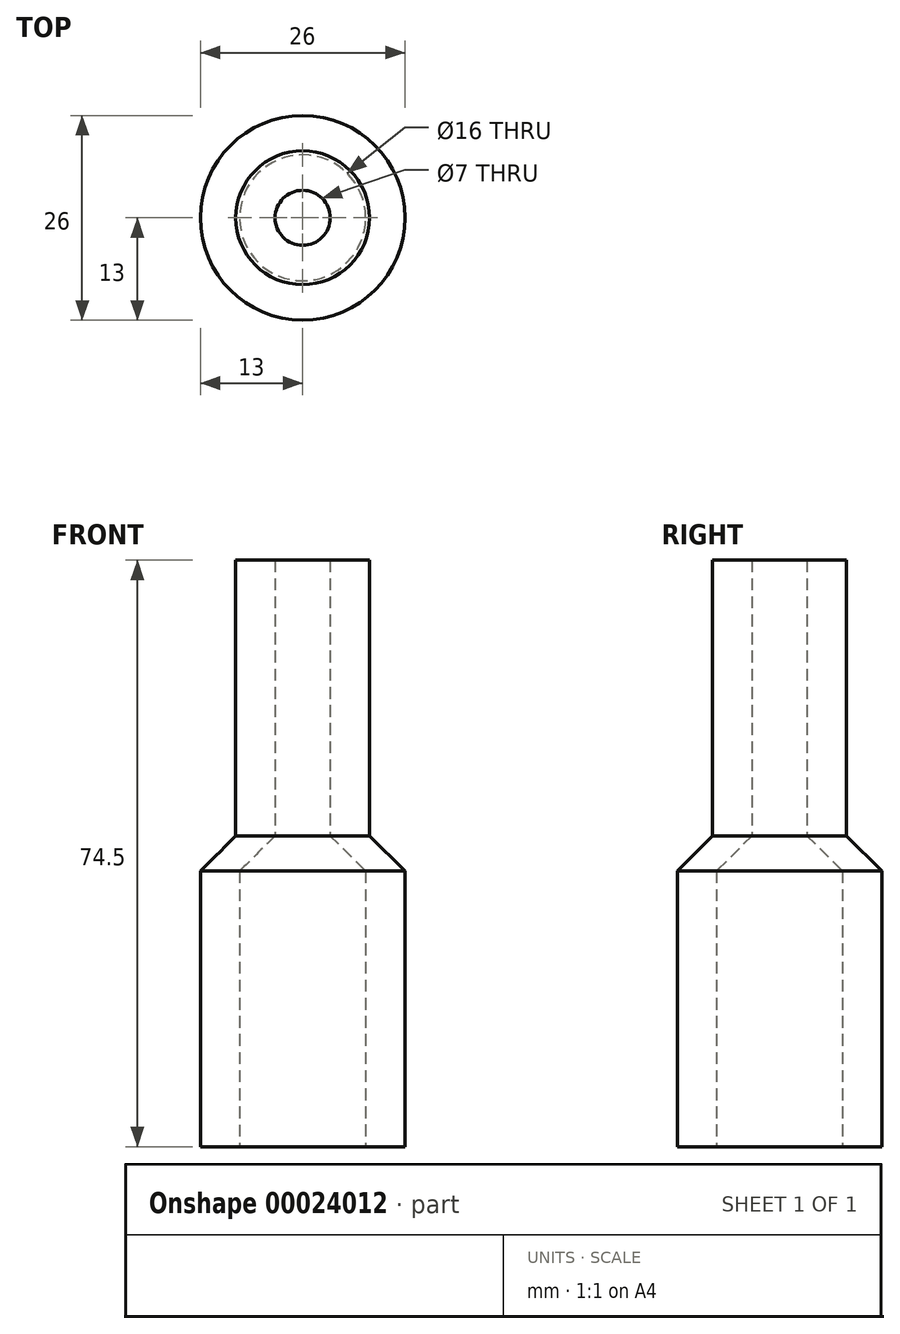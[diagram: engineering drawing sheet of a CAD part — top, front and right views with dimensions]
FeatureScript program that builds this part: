
annotation { "Feature Type Name" : "Feature", "Feature Type Description" : "" }
export const myFeature = defineFeature(function(context is Context, id is Id, definition is map)
    precondition{}
    {
        {
            var Q0;
            Q0=qCreatedBy(makeId("Right.planeOp"),FACE);
            var sketch = newSketch(context, id + "F0", { "sketchPlane" : qUnion([Q0])});
            skLineSegment(sketch, "E0", {"start": v(8, 0) * mm, "end": v(13, 0) * mm});
            skLineSegment(sketch, "E1", {"start": v(13, 0) * mm, "end": v(13, 35) * mm});
            skLineSegment(sketch, "E2", {"start": v(8, 0) * mm, "end": v(8, 35) * mm});
            skLineSegment(sketch, "E3", {"start": v(8, 35) * mm, "end": v(3.5, 39.5) * mm});
            skLineSegment(sketch, "E4", {"start": v(3.5, 39.5) * mm, "end": v(3.5, 74.5) * mm});
            skLineSegment(sketch, "E5", {"start": v(3.5, 74.5) * mm, "end": v(8.5, 74.5) * mm});
            skLineSegment(sketch, "E6", {"start": v(8.5, 74.5) * mm, "end": v(8.5, 39.47) * mm});
            skLineSegment(sketch, "E7", {"start": v(8.5, 39.47) * mm, "end": v(13, 35) * mm});
            skLineSegment(sketch, "E8", {"start": v(0, 0) * mm, "end": v(0, 75.99) * mm});
            skSolve(sketch);
        }
        {
            var Q0;
            Q0=makeQuery(id+"F0.imprint","IMPRINT",FACE,{"disambiguationData":[TD([[makeQuery(id+"F0.imprint","IMPRINT",EDGE,{"derivedFrom":sQuery(id+"F0.wireOp",EDGE,"E0")}),1.0]])]});
            var Q1;
            Q1=sQuery(id+"F0.wireOp",EDGE,"E8");
            revolve(context, id + "F1", {"entities" : qUnion([Q0]), "axis" : qUnion([Q1]), "revolveType" : RevolveType.FULL});
        }
    });
